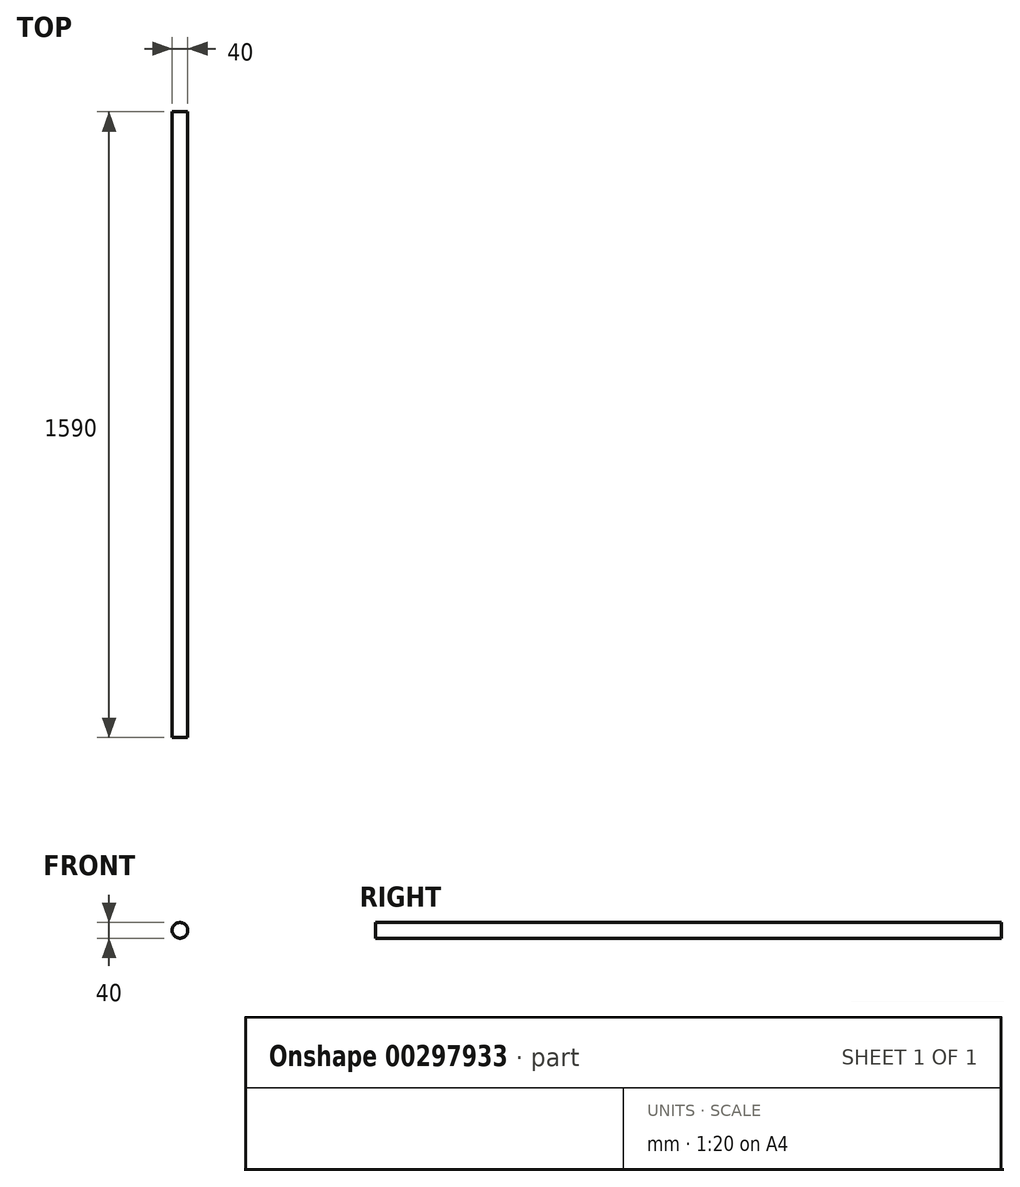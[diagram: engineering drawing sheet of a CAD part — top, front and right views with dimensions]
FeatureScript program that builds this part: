
annotation { "Feature Type Name" : "Feature", "Feature Type Description" : "" }
export const myFeature = defineFeature(function(context is Context, id is Id, definition is map)
    precondition{}
    {
        {
            var Q0;
            Q0=qCreatedBy(makeId("Front.planeOp"),FACE);
            var sketch = newSketch(context, id + "F0", { "sketchPlane" : qUnion([Q0])});
            skCircle(sketch, "E0", {"center": v(0, 0) * mm, "radius": 20 * mm});
            skSolve(sketch);
        }
        {
            var Q0;
            Q0=makeQuery(id+"F0.imprint","IMPRINT",FACE,{"disambiguationData":[TD([[makeQuery(id+"F0.imprint","IMPRINT",EDGE,{"derivedFrom":sQuery(id+"F0.wireOp",EDGE,"E0")}),1.0]])]});
            extrude(context, id + "F1", {"entities" : qUnion([Q0]), "endBound" : BoundingType.SYMMETRIC, "depth" : 1590 * mm});
        }
    });
